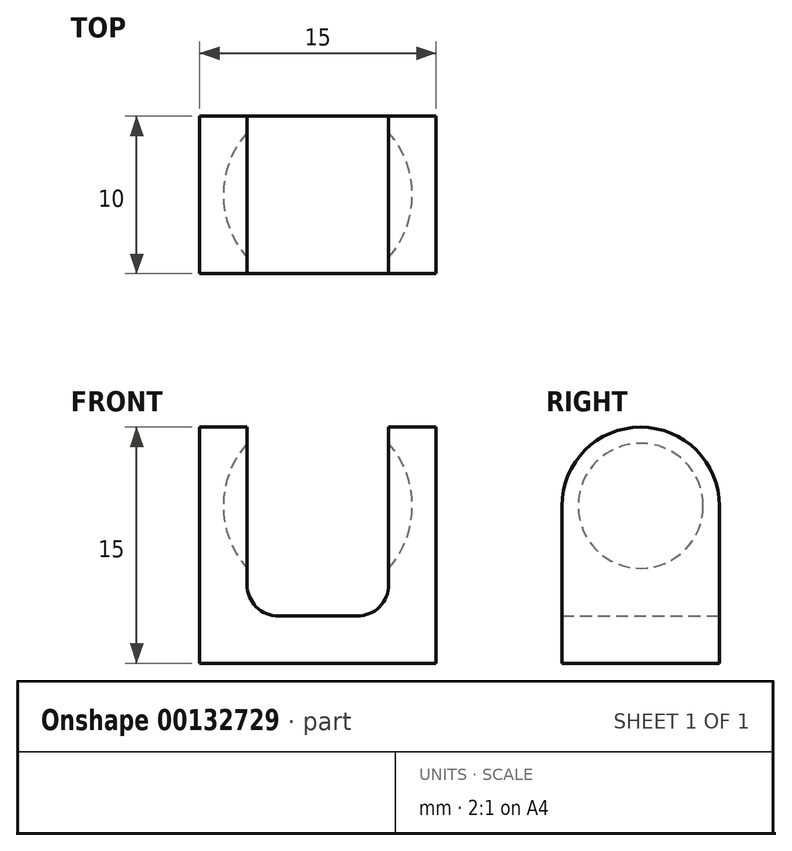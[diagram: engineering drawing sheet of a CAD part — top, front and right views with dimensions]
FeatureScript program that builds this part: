
annotation { "Feature Type Name" : "Feature", "Feature Type Description" : "" }
export const myFeature = defineFeature(function(context is Context, id is Id, definition is map)
    precondition{}
    {
        {
            var Q0;
            Q0=qCreatedBy(makeId("Front.planeOp"),FACE);
            var sketch = newSketch(context, id + "F0", { "sketchPlane" : qUnion([Q0])});
            skArc(sketch, "E0", {"start": v(0, 6) * mm, "mid": v(-6, 0) * mm, "end": v(0, -6) * mm});
            skLineSegment(sketch, "E1", {"start": v(0, 6) * mm, "end": v(0, -6) * mm});
            skLineSegment(sketch, "E2", {"start": v(0, -7) * mm, "end": v(-4.5, -7) * mm});
            skLineSegment(sketch, "E3", {"start": v(-4.5, -7) * mm, "end": v(-4.5, 5) * mm});
            skLineSegment(sketch, "E4", {"start": v(-4.5, 5) * mm, "end": v(-7.5, 5) * mm});
            skLineSegment(sketch, "E5", {"start": v(-7.5, 5) * mm, "end": v(-7.5, -10) * mm});
            skLineSegment(sketch, "E6", {"start": v(-7.5, -10) * mm, "end": v(0, -10) * mm});
            skLineSegment(sketch, "E7", {"start": v(0, -10) * mm, "end": v(0, -7) * mm});
            skLineSegment(sketch, "E8.MirrorCS", {"start": v(7.5, -10) * mm, "end": v(0, -10) * mm});
            skLineSegment(sketch, "E9.MirrorCS", {"start": v(0, -7) * mm, "end": v(4.5, -7) * mm});
            skLineSegment(sketch, "E10.MirrorCS", {"start": v(4.5, -7) * mm, "end": v(4.5, 5) * mm});
            skLineSegment(sketch, "E11.MirrorCS", {"start": v(4.5, 5) * mm, "end": v(7.5, 5) * mm});
            skLineSegment(sketch, "E12.MirrorCS", {"start": v(7.5, 5) * mm, "end": v(7.5, -10) * mm});
            skSolve(sketch);
        }
        {
            var Q0;
            Q0=makeQuery(id+"F0.imprint","IMPRINT",FACE,{"disambiguationData":[TD([[makeQuery(id+"F0.imprint","IMPRINT",EDGE,{"derivedFrom":sQuery(id+"F0.wireOp",EDGE,"E7")}),-1.0]])]});
            var Q1;
            {var subQ4=sQuery(id+"F0.wireOp",EDGE,"E2");Q1=makeQuery(id+"F0.imprint","IMPRINT",FACE,{"disambiguationData":[TD([[makeQuery(id+"F0.imprint","IMPRINT",EDGE,{"derivedFrom":subQ4}),1.0]])]});}
            var Q2;
            {var subQ0=sQuery(id+"F0.wireOp",EDGE,"E3");var subQ1=sQuery(id+"F0.wireOp",EDGE,"E0");var subQ2=makeQuery(id+"F0.imprint","INTERSECT",VERTEX,{"disambiguationData":[OD(0.0)],"derivedFrom":[subQ1,subQ0]});Q2=makeQuery(id+"F0.imprint","IMPRINT",FACE,{"disambiguationData":[TD([[makeQuery(id+"F0.imprint","IMPRINT",EDGE,{"disambiguationData":[TD([[subQ2,-1.0]])],"derivedFrom":subQ1}),1.0]])]});}
            extrude(context, id + "F1", {"entities" : qUnion([Q0, Q1, Q2]), "endBound" : BoundingType.SYMMETRIC, "depth" : 10 * mm});
        }
        {
            var Q0;
            {var subQ0=sQuery(id+"F0.wireOp",EDGE,"E1");Q0=makeQuery(id+"F0.imprint","IMPRINT",FACE,{"disambiguationData":[TD([[makeQuery(id+"F0.imprint","IMPRINT",EDGE,{"derivedFrom":subQ0}),-1.0]])]});}
            var Q1;
            {var subQ0=sQuery(id+"F0.wireOp",EDGE,"E3");var subQ1=sQuery(id+"F0.wireOp",EDGE,"E0");var subQ2=makeQuery(id+"F0.imprint","INTERSECT",VERTEX,{"disambiguationData":[OD(0.0)],"derivedFrom":[subQ1,subQ0]});Q1=makeQuery(id+"F0.imprint","IMPRINT",FACE,{"disambiguationData":[TD([[makeQuery(id+"F0.imprint","IMPRINT",EDGE,{"disambiguationData":[TD([[subQ2,-1.0]])],"derivedFrom":subQ1}),1.0]])]});}
            var Q2;
            Q2=sQuery(id+"F0.wireOp",EDGE,"E1");
            revolve(context, id + "F2", {"operationType" : NewBodyOperationType.REMOVE, "entities" : qUnion([Q0, Q1]), "axis" : qUnion([Q2]), "revolveType" : RevolveType.FULL, "oppositeDirection" : true});
        }
        {
            var Q0;
            Q0=makeQuery(id+"F1.opExtrude","SWEPT_EDGE",EDGE,{"disambiguationData":[OSD([sQuery(id+"F0.wireOp",EDGE,"E2"),sQuery(id+"F0.wireOp",EDGE,"E3")])]});
            var Q1;
            Q1=makeQuery(id+"F1.opExtrude","SWEPT_EDGE",EDGE,{"disambiguationData":[OSD([sQuery(id+"F0.wireOp",EDGE,"E9.MirrorCS"),sQuery(id+"F0.wireOp",EDGE,"E10.MirrorCS")])]});
            fillet(context, id + "F3", {"entities" : qUnion([Q0, Q1]), "radius" : 2 * mm, "allowEdgeOverflow" : false});
        }
        {
            var Q0;
            Q0=makeQuery(id+"F1.opExtrude","CAP_EDGE",EDGE,{"disambiguationData":[OSD([sQuery(id+"F0.wireOp",EDGE,"E11.MirrorCS")])],"isStart":false});
            var Q1;
            Q1=makeQuery(id+"F1.opExtrude","CAP_EDGE",EDGE,{"disambiguationData":[OSD([sQuery(id+"F0.wireOp",EDGE,"E11.MirrorCS")])],"isStart":true});
            var Q2;
            Q2=makeQuery(id+"F1.opExtrude","CAP_EDGE",EDGE,{"disambiguationData":[OSD([sQuery(id+"F0.wireOp",EDGE,"E4")])],"isStart":true});
            var Q3;
            Q3=makeQuery(id+"F1.opExtrude","CAP_EDGE",EDGE,{"disambiguationData":[OSD([sQuery(id+"F0.wireOp",EDGE,"E4")])],"isStart":false});
            fillet(context, id + "F4", {"entities" : qUnion([Q0, Q1, Q2, Q3]), "radius" : 5 * mm, "allowEdgeOverflow" : false});
        }
    });
